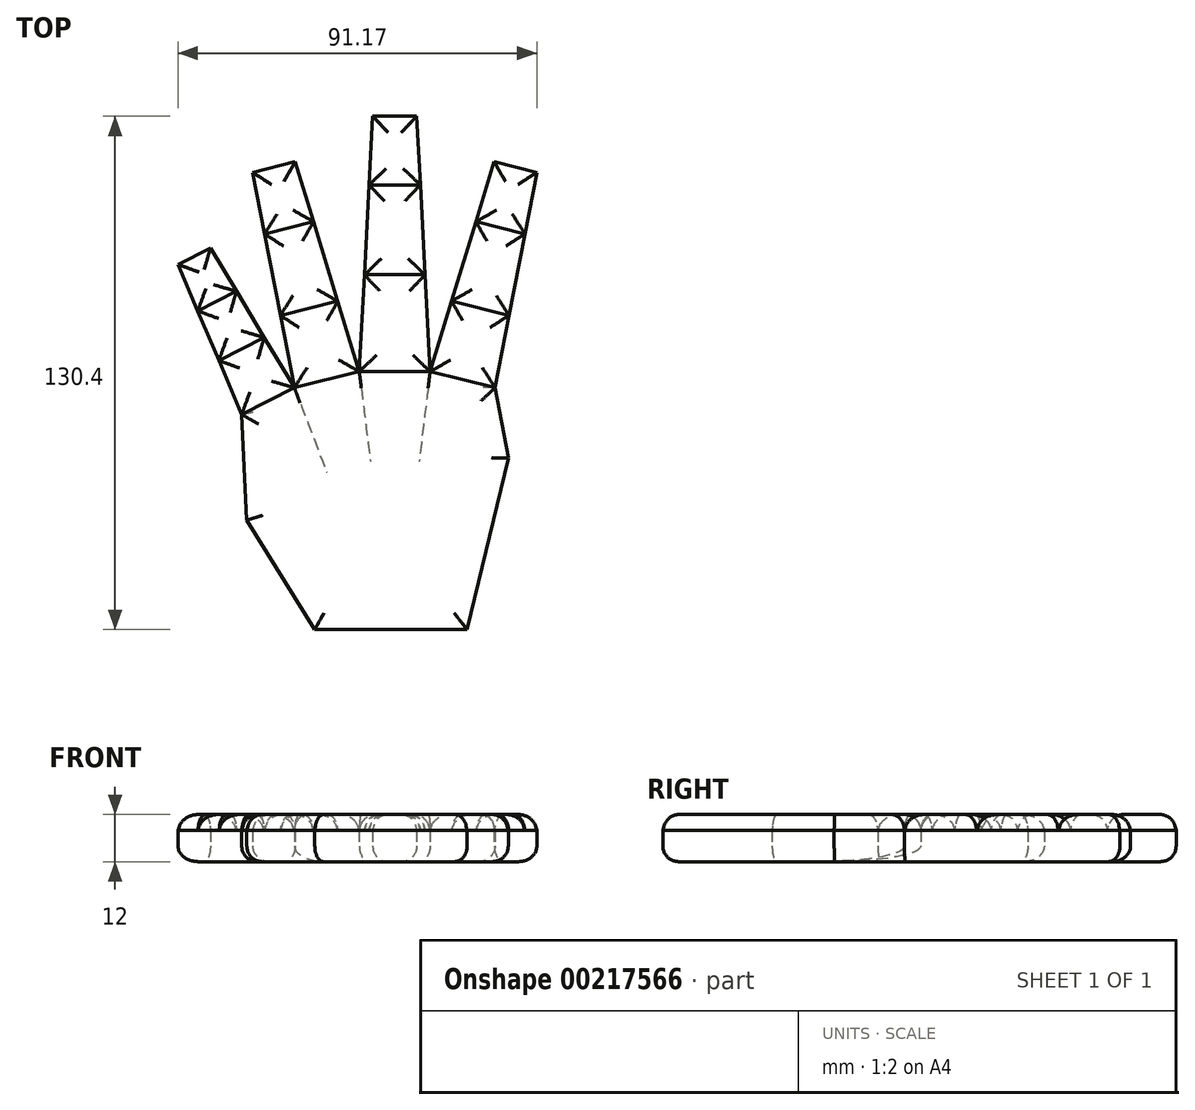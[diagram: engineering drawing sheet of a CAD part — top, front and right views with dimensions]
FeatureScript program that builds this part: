
annotation { "Feature Type Name" : "Feature", "Feature Type Description" : "" }
export const myFeature = defineFeature(function(context is Context, id is Id, definition is map)
    precondition{}
    {
        {
            var Q0;
            Q0=qCreatedBy(makeId("Top.planeOp"),FACE);
            var sketch = newSketch(context, id + "F0", { "sketchPlane" : qUnion([Q0])});
            skLineSegment(sketch, "E0", {"start": v(25.5, -4.11) * mm, "end": v(9, 0) * mm});
            skLineSegment(sketch, "E1", {"start": v(9, 0) * mm, "end": v(-9, 0) * mm});
            skLineSegment(sketch, "E2", {"start": v(-9, 0) * mm, "end": v(-25.5, -4.11) * mm});
            skLineSegment(sketch, "E3", {"start": v(-25.5, -4.11) * mm, "end": v(-38.86, -10.92) * mm});
            skLineSegment(sketch, "E4", {"start": v(-38.86, -10.92) * mm, "end": v(-37.58, -37.78) * mm});
            skLineSegment(sketch, "E5", {"start": v(-37.58, -37.78) * mm, "end": v(-20.3, -65.54) * mm});
            skLineSegment(sketch, "E6", {"start": v(-20.3, -65.54) * mm, "end": v(18.4, -65.54) * mm});
            skLineSegment(sketch, "E7", {"start": v(18.4, -65.54) * mm, "end": v(36.52, -48.36) * mm});
            skLineSegment(sketch, "E8", {"start": v(36.52, -48.36) * mm, "end": v(32.62, -24.73) * mm});
            skLineSegment(sketch, "E9", {"start": v(32.62, -24.73) * mm, "end": v(28.86, -22.02) * mm});
            skLineSegment(sketch, "E10", {"start": v(25.5, -4.11) * mm, "end": v(36.13, 50.58) * mm});
            skLineSegment(sketch, "E11", {"start": v(36.13, 50.58) * mm, "end": v(25.3, 53.28) * mm});
            skLineSegment(sketch, "E12", {"start": v(25.3, 53.28) * mm, "end": v(9, 0) * mm});
            skLineSegment(sketch, "E13", {"start": v(9, 0) * mm, "end": v(5.6, 64.86) * mm});
            skLineSegment(sketch, "E14", {"start": v(5.6, 64.86) * mm, "end": v(-5.6, 64.86) * mm});
            skLineSegment(sketch, "E15", {"start": v(-5.6, 64.86) * mm, "end": v(-9, 0) * mm});
            skLineSegment(sketch, "E16", {"start": v(-9, 0) * mm, "end": v(-25.3, 53.28) * mm});
            skLineSegment(sketch, "E17", {"start": v(-25.3, 53.28) * mm, "end": v(-36.13, 50.58) * mm});
            skLineSegment(sketch, "E18", {"start": v(-36.13, 50.58) * mm, "end": v(-25.5, -4.11) * mm});
            skLineSegment(sketch, "E19", {"start": v(-25.5, -4.11) * mm, "end": v(-46.82, 31.38) * mm});
            skLineSegment(sketch, "E20", {"start": v(-46.82, 31.38) * mm, "end": v(-55.04, 27.2) * mm});
            skLineSegment(sketch, "E21", {"start": v(-55.04, 27.2) * mm, "end": v(-38.86, -10.92) * mm});
            skLineSegment(sketch, "E22", {"start": v(32.62, -24.73) * mm, "end": v(46.6, -20.32) * mm});
            skLineSegment(sketch, "E23", {"start": v(46.6, -20.32) * mm, "end": v(51.49, -32.7) * mm});
            skLineSegment(sketch, "E24", {"start": v(51.49, -32.7) * mm, "end": v(36.52, -48.36) * mm});
            skLineSegment(sketch, "E25", {"start": v(51.49, -32.7) * mm, "end": v(64.06, -17.7) * mm});
            skLineSegment(sketch, "E26", {"start": v(64.06, -17.7) * mm, "end": v(58.4, -11.06) * mm});
            skLineSegment(sketch, "E27", {"start": v(58.4, -11.06) * mm, "end": v(46.6, -20.32) * mm});
            skLineSegment(sketch, "E28", {"start": v(64.06, -17.7) * mm, "end": v(72.07, -13.2) * mm});
            skLineSegment(sketch, "E29", {"start": v(72.07, -13.2) * mm, "end": v(79.26, -11.05) * mm});
            skLineSegment(sketch, "E30", {"start": v(79.26, -11.05) * mm, "end": v(78.24, -5.68) * mm});
            skLineSegment(sketch, "E31", {"start": v(78.24, -5.68) * mm, "end": v(67.97, -5.78) * mm});
            skLineSegment(sketch, "E32", {"start": v(67.97, -5.78) * mm, "end": v(58.4, -11.06) * mm});
            skLineSegment(sketch, "E33", {"start": v(-32.18, -7.52) * mm, "end": v(-50.93, 29.28) * mm, "construction": true});
            skLineSegment(sketch, "E34", {"start": v(-17.25, -2.06) * mm, "end": v(-30.7, 51.93) * mm, "construction": true});
            skLineSegment(sketch, "E35", {"start": v(0, 0) * mm, "end": v(0, 64.86) * mm, "construction": true});
            skLineSegment(sketch, "E36", {"start": v(17.25, -2.06) * mm, "end": v(30.7, 51.93) * mm, "construction": true});
            skLineSegment(sketch, "E37", {"start": v(28.86, -22.02) * mm, "end": v(25.5, -4.11) * mm});
            skLineSegment(sketch, "E38", {"start": v(29.06, 14.23) * mm, "end": v(14.46, 17.87) * mm});
            skLineSegment(sketch, "E39", {"start": v(7.71, 24.58) * mm, "end": v(-7.71, 24.58) * mm});
            skLineSegment(sketch, "E40", {"start": v(-14.46, 17.87) * mm, "end": v(-29.06, 14.23) * mm});
            skLineSegment(sketch, "E41", {"start": v(-33.17, 8.66) * mm, "end": v(-44.68, 2.79) * mm});
            skLineSegment(sketch, "E42", {"start": v(-40.21, 20.38) * mm, "end": v(-50.02, 15.38) * mm});
            skLineSegment(sketch, "E43", {"start": v(-20.64, 38.06) * mm, "end": v(-33.09, 34.96) * mm});
            skLineSegment(sketch, "E44", {"start": v(33.09, 34.96) * mm, "end": v(20.64, 38.06) * mm});
            skLineSegment(sketch, "E45", {"start": v(6.52, 47.41) * mm, "end": v(-6.52, 47.41) * mm});
            skLineSegment(sketch, "E46", {"start": v(28.86, -22.02) * mm, "end": v(18.4, -65.54) * mm});
            skSolve(sketch);
        }
        {
            var Q0;
            {var subQ0=sQuery(id+"F0.wireOp",EDGE,"E3");Q0=makeQuery(id+"F0.imprint","IMPRINT",FACE,{"disambiguationData":[TD([[makeQuery(id+"F0.imprint","IMPRINT",EDGE,{"derivedFrom":subQ0}),-1.0]])]});}
            var Q1;
            {var subQ0=sQuery(id+"F0.wireOp",EDGE,"E2");Q1=makeQuery(id+"F0.imprint","IMPRINT",FACE,{"disambiguationData":[TD([[makeQuery(id+"F0.imprint","IMPRINT",EDGE,{"derivedFrom":subQ0}),-1.0]])]});}
            var Q2;
            {var subQ0=sQuery(id+"F0.wireOp",EDGE,"E1");Q2=makeQuery(id+"F0.imprint","IMPRINT",FACE,{"disambiguationData":[TD([[makeQuery(id+"F0.imprint","IMPRINT",EDGE,{"derivedFrom":subQ0}),-1.0]])]});}
            var Q3;
            {var subQ0=sQuery(id+"F0.wireOp",EDGE,"E0");Q3=makeQuery(id+"F0.imprint","IMPRINT",FACE,{"disambiguationData":[TD([[makeQuery(id+"F0.imprint","IMPRINT",EDGE,{"derivedFrom":subQ0}),-1.0]])]});}
            var Q4;
            {var subQ0=sQuery(id+"F0.wireOp",EDGE,"E11");Q4=makeQuery(id+"F0.imprint","IMPRINT",FACE,{"disambiguationData":[TD([[makeQuery(id+"F0.imprint","IMPRINT",EDGE,{"derivedFrom":subQ0}),1.0]])]});}
            var Q5;
            {var subQ0=sQuery(id+"F0.wireOp",EDGE,"E14");Q5=makeQuery(id+"F0.imprint","IMPRINT",FACE,{"disambiguationData":[TD([[makeQuery(id+"F0.imprint","IMPRINT",EDGE,{"derivedFrom":subQ0}),1.0]])]});}
            var Q6;
            {var subQ0=sQuery(id+"F0.wireOp",EDGE,"E17");Q6=makeQuery(id+"F0.imprint","IMPRINT",FACE,{"disambiguationData":[TD([[makeQuery(id+"F0.imprint","IMPRINT",EDGE,{"derivedFrom":subQ0}),1.0]])]});}
            var Q7;
            {var subQ0=sQuery(id+"F0.wireOp",EDGE,"E20");Q7=makeQuery(id+"F0.imprint","IMPRINT",FACE,{"disambiguationData":[TD([[makeQuery(id+"F0.imprint","IMPRINT",EDGE,{"derivedFrom":subQ0}),1.0]])]});}
            extrude(context, id + "F1", {"entities" : qUnion([Q0, Q1, Q2, Q3, Q4, Q5, Q6, Q7]), "endBound" : BoundingType.SYMMETRIC, "depth" : 8 * mm});
        }
        {
            var Q0;
            {var subQ0=sQuery(id+"F0.wireOp",EDGE,"E41");Q0=makeQuery(id+"F0.imprint","IMPRINT",FACE,{"disambiguationData":[TD([[makeQuery(id+"F0.imprint","IMPRINT",EDGE,{"derivedFrom":subQ0}),-1.0]])]});}
            var Q1;
            {var subQ0=sQuery(id+"F0.wireOp",EDGE,"E40");Q1=makeQuery(id+"F0.imprint","IMPRINT",FACE,{"disambiguationData":[TD([[makeQuery(id+"F0.imprint","IMPRINT",EDGE,{"derivedFrom":subQ0}),-1.0]])]});}
            var Q2;
            {var subQ0=sQuery(id+"F0.wireOp",EDGE,"E39");Q2=makeQuery(id+"F0.imprint","IMPRINT",FACE,{"disambiguationData":[TD([[makeQuery(id+"F0.imprint","IMPRINT",EDGE,{"derivedFrom":subQ0}),-1.0]])]});}
            var Q3;
            {var subQ0=sQuery(id+"F0.wireOp",EDGE,"E38");Q3=makeQuery(id+"F0.imprint","IMPRINT",FACE,{"disambiguationData":[TD([[makeQuery(id+"F0.imprint","IMPRINT",EDGE,{"derivedFrom":subQ0}),-1.0]])]});}
            var Q4;
            Q4=makeQuery(id+"F0.imprint","IMPRINT",FACE,{"disambiguationData":[TD([[makeQuery(id+"F0.imprint","IMPRINT",EDGE,{"derivedFrom":sQuery(id+"F0.wireOp",EDGE,"E0")}),1.0]])]});
            extrude(context, id + "F2", {"entities" : qUnion([Q0, Q1, Q2, Q3, Q4]), "endBound" : BoundingType.SYMMETRIC, "depth" : 8 * mm});
        }
        {
            var Q0;
            Q0=makeQuery(id+"F1.opExtrude","CAP_FACE",FACE,{"disambiguationData":[OSD([sQuery(id+"F0.wireOp",EDGE,"E0"),sQuery(id+"F0.wireOp",EDGE,"E10"),sQuery(id+"F0.wireOp",EDGE,"E12"),sQuery(id+"F0.wireOp",EDGE,"E38")])],"isStart":false});
            var Q1;
            Q1=makeQuery(id+"F1.opExtrude","CAP_FACE",FACE,{"disambiguationData":[OSD([sQuery(id+"F0.wireOp",EDGE,"E10"),sQuery(id+"F0.wireOp",EDGE,"E11"),sQuery(id+"F0.wireOp",EDGE,"E12"),sQuery(id+"F0.wireOp",EDGE,"E44")])],"isStart":false});
            var Q2;
            Q2=makeQuery(id+"F1.opExtrude","CAP_FACE",FACE,{"disambiguationData":[OSD([sQuery(id+"F0.wireOp",EDGE,"E13"),sQuery(id+"F0.wireOp",EDGE,"E14"),sQuery(id+"F0.wireOp",EDGE,"E15"),sQuery(id+"F0.wireOp",EDGE,"E45")])],"isStart":false});
            var Q3;
            Q3=makeQuery(id+"F1.opExtrude","CAP_FACE",FACE,{"disambiguationData":[OSD([sQuery(id+"F0.wireOp",EDGE,"E1"),sQuery(id+"F0.wireOp",EDGE,"E13"),sQuery(id+"F0.wireOp",EDGE,"E15"),sQuery(id+"F0.wireOp",EDGE,"E39")])],"isStart":false});
            var Q4;
            Q4=makeQuery(id+"F1.opExtrude","CAP_FACE",FACE,{"disambiguationData":[OSD([sQuery(id+"F0.wireOp",EDGE,"E16"),sQuery(id+"F0.wireOp",EDGE,"E17"),sQuery(id+"F0.wireOp",EDGE,"E18"),sQuery(id+"F0.wireOp",EDGE,"E43")])],"isStart":false});
            var Q5;
            Q5=makeQuery(id+"F1.opExtrude","CAP_FACE",FACE,{"disambiguationData":[OSD([sQuery(id+"F0.wireOp",EDGE,"E2"),sQuery(id+"F0.wireOp",EDGE,"E16"),sQuery(id+"F0.wireOp",EDGE,"E18"),sQuery(id+"F0.wireOp",EDGE,"E40")])],"isStart":false});
            var Q6;
            Q6=makeQuery(id+"F1.opExtrude","CAP_FACE",FACE,{"disambiguationData":[OSD([sQuery(id+"F0.wireOp",EDGE,"E19"),sQuery(id+"F0.wireOp",EDGE,"E20"),sQuery(id+"F0.wireOp",EDGE,"E21"),sQuery(id+"F0.wireOp",EDGE,"E42")])],"isStart":false});
            var Q7;
            Q7=makeQuery(id+"F1.opExtrude","CAP_FACE",FACE,{"disambiguationData":[OSD([sQuery(id+"F0.wireOp",EDGE,"E3"),sQuery(id+"F0.wireOp",EDGE,"E19"),sQuery(id+"F0.wireOp",EDGE,"E21"),sQuery(id+"F0.wireOp",EDGE,"E41")])],"isStart":false});
            extrude(context, id + "F3", {"entities" : qUnion([Q0, Q1, Q2, Q3, Q4, Q5, Q6, Q7]), "operationType" : NewBodyOperationType.ADD, "depth" : 4 * mm, "hasDraft" : true, "draftAngle" : 15 * degree, "draftPullDirection" : true});
        }
        {
            var Q0;
            Q0=makeQuery(id+"F2.opExtrude","CAP_FACE",FACE,{"disambiguationData":[OSD([sQuery(id+"F0.wireOp",EDGE,"E10"),sQuery(id+"F0.wireOp",EDGE,"E12"),sQuery(id+"F0.wireOp",EDGE,"E38"),sQuery(id+"F0.wireOp",EDGE,"E44")])],"isStart":false});
            var Q1;
            Q1=makeQuery(id+"F2.opExtrude","CAP_FACE",FACE,{"disambiguationData":[OSD([sQuery(id+"F0.wireOp",EDGE,"E13"),sQuery(id+"F0.wireOp",EDGE,"E15"),sQuery(id+"F0.wireOp",EDGE,"E39"),sQuery(id+"F0.wireOp",EDGE,"E45")])],"isStart":false});
            var Q2;
            Q2=makeQuery(id+"F2.opExtrude","CAP_FACE",FACE,{"disambiguationData":[OSD([sQuery(id+"F0.wireOp",EDGE,"E16"),sQuery(id+"F0.wireOp",EDGE,"E18"),sQuery(id+"F0.wireOp",EDGE,"E40"),sQuery(id+"F0.wireOp",EDGE,"E43")])],"isStart":false});
            var Q3;
            Q3=makeQuery(id+"F2.opExtrude","CAP_FACE",FACE,{"disambiguationData":[OSD([sQuery(id+"F0.wireOp",EDGE,"E19"),sQuery(id+"F0.wireOp",EDGE,"E21"),sQuery(id+"F0.wireOp",EDGE,"E41"),sQuery(id+"F0.wireOp",EDGE,"E42")])],"isStart":false});
            var Q4;
            Q4=makeQuery(id+"F2.opExtrude","CAP_FACE",FACE,{"disambiguationData":[OSD([sQuery(id+"F0.wireOp",EDGE,"E0"),sQuery(id+"F0.wireOp",EDGE,"E1"),sQuery(id+"F0.wireOp",EDGE,"E2"),sQuery(id+"F0.wireOp",EDGE,"E3"),sQuery(id+"F0.wireOp",EDGE,"E4"),sQuery(id+"F0.wireOp",EDGE,"E5"),sQuery(id+"F0.wireOp",EDGE,"E6"),sQuery(id+"F0.wireOp",EDGE,"E37"),sQuery(id+"F0.wireOp",EDGE,"E46")])],"isStart":false});
            extrude(context, id + "F4", {"entities" : qUnion([Q0, Q1, Q2, Q3, Q4]), "operationType" : NewBodyOperationType.ADD, "depth" : 4 * mm, "hasDraft" : true, "draftAngle" : 15 * degree, "draftPullDirection" : true});
        }
        {
            var Q0;
            Q0=makeQuery(id+"F3.opExtrude","CAP_FACE",FACE,{"disambiguationData":[OSD([sQuery(id+"F0.wireOp",EDGE,"E13"),sQuery(id+"F0.wireOp",EDGE,"E14"),sQuery(id+"F0.wireOp",EDGE,"E15"),sQuery(id+"F0.wireOp",EDGE,"E45")])],"isStart":false});
            var Q1;
            Q1=makeQuery(id+"F3.opExtrude","CAP_FACE",FACE,{"disambiguationData":[OSD([sQuery(id+"F0.wireOp",EDGE,"E10"),sQuery(id+"F0.wireOp",EDGE,"E11"),sQuery(id+"F0.wireOp",EDGE,"E12"),sQuery(id+"F0.wireOp",EDGE,"E44")])],"isStart":false});
            var Q2;
            Q2=makeQuery(id+"F4.opExtrude","CAP_FACE",FACE,{"disambiguationData":[OSD([sQuery(id+"F0.wireOp",EDGE,"E10"),sQuery(id+"F0.wireOp",EDGE,"E12"),sQuery(id+"F0.wireOp",EDGE,"E38"),sQuery(id+"F0.wireOp",EDGE,"E44")])],"isStart":false});
            var Q3;
            Q3=makeQuery(id+"F4.opExtrude","CAP_FACE",FACE,{"disambiguationData":[OSD([sQuery(id+"F0.wireOp",EDGE,"E13"),sQuery(id+"F0.wireOp",EDGE,"E15"),sQuery(id+"F0.wireOp",EDGE,"E39"),sQuery(id+"F0.wireOp",EDGE,"E45")])],"isStart":false});
            var Q4;
            Q4=makeQuery(id+"F3.opExtrude","CAP_FACE",FACE,{"disambiguationData":[OSD([sQuery(id+"F0.wireOp",EDGE,"E1"),sQuery(id+"F0.wireOp",EDGE,"E13"),sQuery(id+"F0.wireOp",EDGE,"E15"),sQuery(id+"F0.wireOp",EDGE,"E39")])],"isStart":false});
            var Q5;
            Q5=makeQuery(id+"F3.opExtrude","CAP_FACE",FACE,{"disambiguationData":[OSD([sQuery(id+"F0.wireOp",EDGE,"E0"),sQuery(id+"F0.wireOp",EDGE,"E10"),sQuery(id+"F0.wireOp",EDGE,"E12"),sQuery(id+"F0.wireOp",EDGE,"E38")])],"isStart":false});
            var Q6;
            Q6=makeQuery(id+"F3.opExtrude","CAP_FACE",FACE,{"disambiguationData":[OSD([sQuery(id+"F0.wireOp",EDGE,"E2"),sQuery(id+"F0.wireOp",EDGE,"E16"),sQuery(id+"F0.wireOp",EDGE,"E18"),sQuery(id+"F0.wireOp",EDGE,"E40")])],"isStart":false});
            var Q7;
            Q7=makeQuery(id+"F4.opExtrude","CAP_FACE",FACE,{"disambiguationData":[OSD([sQuery(id+"F0.wireOp",EDGE,"E16"),sQuery(id+"F0.wireOp",EDGE,"E18"),sQuery(id+"F0.wireOp",EDGE,"E40"),sQuery(id+"F0.wireOp",EDGE,"E43")])],"isStart":false});
            var Q8;
            Q8=makeQuery(id+"F3.opExtrude","CAP_FACE",FACE,{"disambiguationData":[OSD([sQuery(id+"F0.wireOp",EDGE,"E16"),sQuery(id+"F0.wireOp",EDGE,"E17"),sQuery(id+"F0.wireOp",EDGE,"E18"),sQuery(id+"F0.wireOp",EDGE,"E43")])],"isStart":false});
            var Q9;
            Q9=makeQuery(id+"F3.opExtrude","CAP_FACE",FACE,{"disambiguationData":[OSD([sQuery(id+"F0.wireOp",EDGE,"E19"),sQuery(id+"F0.wireOp",EDGE,"E20"),sQuery(id+"F0.wireOp",EDGE,"E21"),sQuery(id+"F0.wireOp",EDGE,"E42")])],"isStart":false});
            var Q10;
            Q10=makeQuery(id+"F4.opExtrude","CAP_FACE",FACE,{"disambiguationData":[OSD([sQuery(id+"F0.wireOp",EDGE,"E19"),sQuery(id+"F0.wireOp",EDGE,"E21"),sQuery(id+"F0.wireOp",EDGE,"E41"),sQuery(id+"F0.wireOp",EDGE,"E42")])],"isStart":false});
            var Q11;
            Q11=makeQuery(id+"F3.opExtrude","CAP_FACE",FACE,{"disambiguationData":[OSD([sQuery(id+"F0.wireOp",EDGE,"E3"),sQuery(id+"F0.wireOp",EDGE,"E19"),sQuery(id+"F0.wireOp",EDGE,"E21"),sQuery(id+"F0.wireOp",EDGE,"E41")])],"isStart":false});
            var Q12;
            Q12=makeQuery(id+"F4.opExtrude","CAP_FACE",FACE,{"disambiguationData":[OSD([sQuery(id+"F0.wireOp",EDGE,"E0"),sQuery(id+"F0.wireOp",EDGE,"E1"),sQuery(id+"F0.wireOp",EDGE,"E2"),sQuery(id+"F0.wireOp",EDGE,"E3"),sQuery(id+"F0.wireOp",EDGE,"E4"),sQuery(id+"F0.wireOp",EDGE,"E5"),sQuery(id+"F0.wireOp",EDGE,"E6"),sQuery(id+"F0.wireOp",EDGE,"E37"),sQuery(id+"F0.wireOp",EDGE,"E46")])],"isStart":false});
            var Q13;
            Q13=makeQuery(id+"F1.opExtrude","CAP_FACE",FACE,{"disambiguationData":[OSD([sQuery(id+"F0.wireOp",EDGE,"E16"),sQuery(id+"F0.wireOp",EDGE,"E17"),sQuery(id+"F0.wireOp",EDGE,"E18"),sQuery(id+"F0.wireOp",EDGE,"E43")])],"isStart":true});
            var Q14;
            Q14=makeQuery(id+"F1.opExtrude","CAP_FACE",FACE,{"disambiguationData":[OSD([sQuery(id+"F0.wireOp",EDGE,"E13"),sQuery(id+"F0.wireOp",EDGE,"E14"),sQuery(id+"F0.wireOp",EDGE,"E15"),sQuery(id+"F0.wireOp",EDGE,"E45")])],"isStart":true});
            var Q15;
            Q15=makeQuery(id+"F1.opExtrude","CAP_FACE",FACE,{"disambiguationData":[OSD([sQuery(id+"F0.wireOp",EDGE,"E10"),sQuery(id+"F0.wireOp",EDGE,"E11"),sQuery(id+"F0.wireOp",EDGE,"E12"),sQuery(id+"F0.wireOp",EDGE,"E44")])],"isStart":true});
            var Q16;
            Q16=makeQuery(id+"F2.opExtrude","CAP_FACE",FACE,{"disambiguationData":[OSD([sQuery(id+"F0.wireOp",EDGE,"E10"),sQuery(id+"F0.wireOp",EDGE,"E12"),sQuery(id+"F0.wireOp",EDGE,"E38"),sQuery(id+"F0.wireOp",EDGE,"E44")])],"isStart":true});
            var Q17;
            Q17=makeQuery(id+"F2.opExtrude","CAP_FACE",FACE,{"disambiguationData":[OSD([sQuery(id+"F0.wireOp",EDGE,"E13"),sQuery(id+"F0.wireOp",EDGE,"E15"),sQuery(id+"F0.wireOp",EDGE,"E39"),sQuery(id+"F0.wireOp",EDGE,"E45")])],"isStart":true});
            var Q18;
            Q18=makeQuery(id+"F2.opExtrude","CAP_FACE",FACE,{"disambiguationData":[OSD([sQuery(id+"F0.wireOp",EDGE,"E16"),sQuery(id+"F0.wireOp",EDGE,"E18"),sQuery(id+"F0.wireOp",EDGE,"E40"),sQuery(id+"F0.wireOp",EDGE,"E43")])],"isStart":true});
            var Q19;
            Q19=makeQuery(id+"F2.opExtrude","CAP_FACE",FACE,{"disambiguationData":[OSD([sQuery(id+"F0.wireOp",EDGE,"E19"),sQuery(id+"F0.wireOp",EDGE,"E21"),sQuery(id+"F0.wireOp",EDGE,"E41"),sQuery(id+"F0.wireOp",EDGE,"E42")])],"isStart":true});
            var Q20;
            Q20=makeQuery(id+"F1.opExtrude","CAP_FACE",FACE,{"disambiguationData":[OSD([sQuery(id+"F0.wireOp",EDGE,"E3"),sQuery(id+"F0.wireOp",EDGE,"E19"),sQuery(id+"F0.wireOp",EDGE,"E21"),sQuery(id+"F0.wireOp",EDGE,"E41")])],"isStart":true});
            var Q21;
            Q21=makeQuery(id+"F1.opExtrude","CAP_FACE",FACE,{"disambiguationData":[OSD([sQuery(id+"F0.wireOp",EDGE,"E2"),sQuery(id+"F0.wireOp",EDGE,"E16"),sQuery(id+"F0.wireOp",EDGE,"E18"),sQuery(id+"F0.wireOp",EDGE,"E40")])],"isStart":true});
            var Q22;
            Q22=makeQuery(id+"F1.opExtrude","CAP_FACE",FACE,{"disambiguationData":[OSD([sQuery(id+"F0.wireOp",EDGE,"E1"),sQuery(id+"F0.wireOp",EDGE,"E13"),sQuery(id+"F0.wireOp",EDGE,"E15"),sQuery(id+"F0.wireOp",EDGE,"E39")])],"isStart":true});
            var Q23;
            Q23=makeQuery(id+"F1.opExtrude","CAP_FACE",FACE,{"disambiguationData":[OSD([sQuery(id+"F0.wireOp",EDGE,"E0"),sQuery(id+"F0.wireOp",EDGE,"E10"),sQuery(id+"F0.wireOp",EDGE,"E12"),sQuery(id+"F0.wireOp",EDGE,"E38")])],"isStart":true});
            var Q24;
            Q24=makeQuery(id+"F2.opExtrude","CAP_FACE",FACE,{"disambiguationData":[OSD([sQuery(id+"F0.wireOp",EDGE,"E0"),sQuery(id+"F0.wireOp",EDGE,"E1"),sQuery(id+"F0.wireOp",EDGE,"E2"),sQuery(id+"F0.wireOp",EDGE,"E3"),sQuery(id+"F0.wireOp",EDGE,"E4"),sQuery(id+"F0.wireOp",EDGE,"E5"),sQuery(id+"F0.wireOp",EDGE,"E6"),sQuery(id+"F0.wireOp",EDGE,"E37"),sQuery(id+"F0.wireOp",EDGE,"E46")])],"isStart":true});
            var Q25;
            Q25=makeQuery(id+"F1.opExtrude","CAP_FACE",FACE,{"disambiguationData":[OSD([sQuery(id+"F0.wireOp",EDGE,"E19"),sQuery(id+"F0.wireOp",EDGE,"E20"),sQuery(id+"F0.wireOp",EDGE,"E21"),sQuery(id+"F0.wireOp",EDGE,"E42")])],"isStart":true});
            fillet(context, id + "F5", {"entities" : qUnion([Q0, Q1, Q2, Q3, Q4, Q5, Q6, Q7, Q8, Q9, Q10, Q11, Q12, Q13, Q14, Q15, Q16, Q17, Q18, Q19, Q20, Q21, Q22, Q23, Q24, Q25]), "radius" : 4 * mm, "tangentPropagation" : true, "allowEdgeOverflow" : false});
        }
    });
